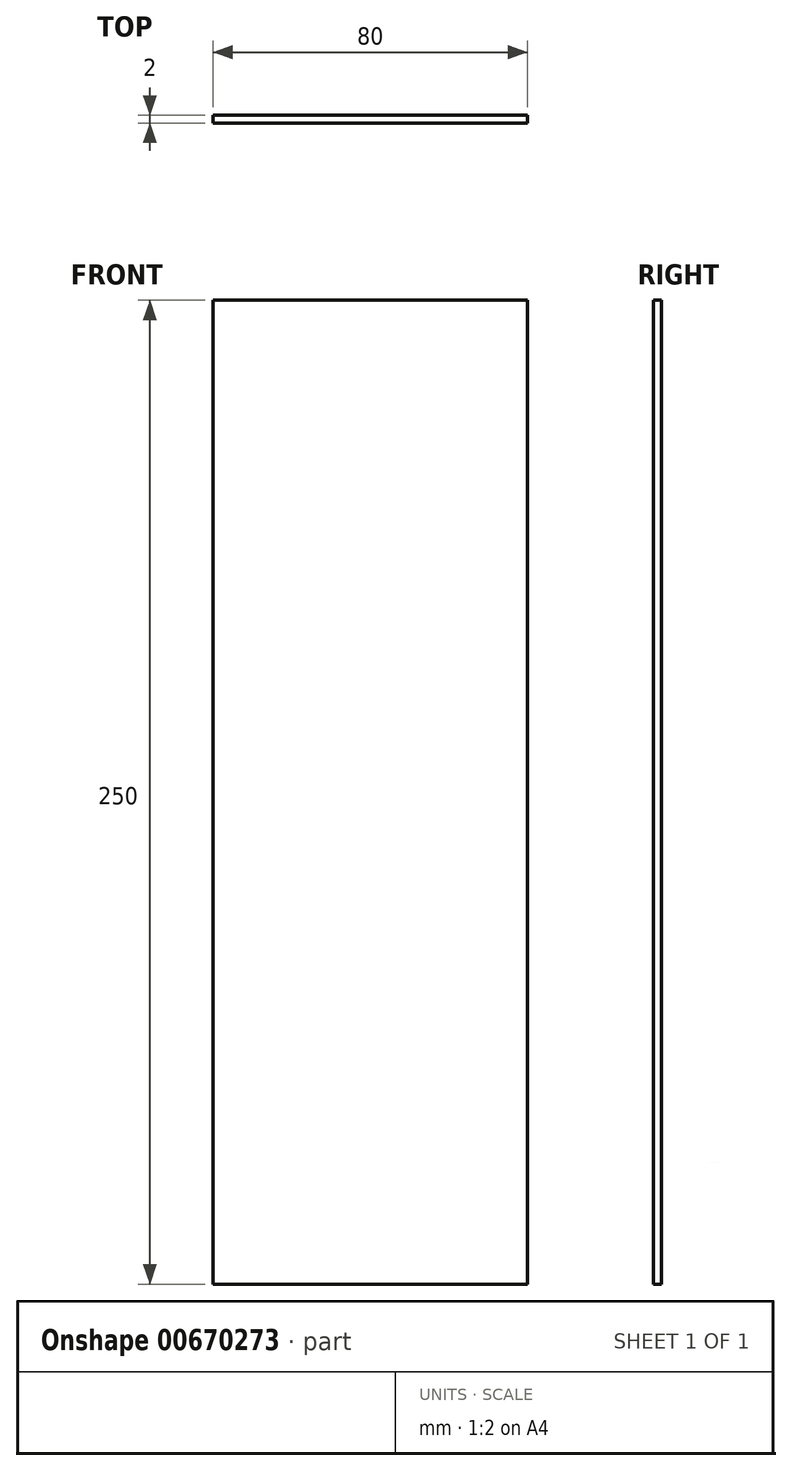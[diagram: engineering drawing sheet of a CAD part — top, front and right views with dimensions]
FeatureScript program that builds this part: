
annotation { "Feature Type Name" : "Feature", "Feature Type Description" : "" }
export const myFeature = defineFeature(function(context is Context, id is Id, definition is map)
    precondition{}
    {
        {
            var Q0;
            Q0=qCreatedBy(makeId("Front.planeOp"),FACE);
            var sketch = newSketch(context, id + "F0", { "sketchPlane" : qUnion([Q0])});
            skLineSegment(sketch, "E0.bottom", {"start": v(-39.17, 179.18) * mm, "end": v(40.83, 179.18) * mm});
            skLineSegment(sketch, "E0.top", {"start": v(-39.17, -70.82) * mm, "end": v(40.83, -70.82) * mm});
            skLineSegment(sketch, "E0.left", {"start": v(-39.17, 179.18) * mm, "end": v(-39.17, -70.82) * mm});
            skLineSegment(sketch, "E0.right", {"start": v(40.83, 179.18) * mm, "end": v(40.83, -70.82) * mm});
            skSolve(sketch);
        }
        {
            var Q0;
            Q0=makeQuery(id+"F0.imprint","IMPRINT",FACE,{"disambiguationData":[TD([[makeQuery(id+"F0.imprint","IMPRINT",EDGE,{"derivedFrom":sQuery(id+"F0.wireOp",EDGE,"E0.bottom")}),-1.0]])]});
            extrude(context, id + "F1", {"entities" : qUnion([Q0]), "depth" : 2 * mm, "offsetDistance" : 25 * mm});
        }
    });
